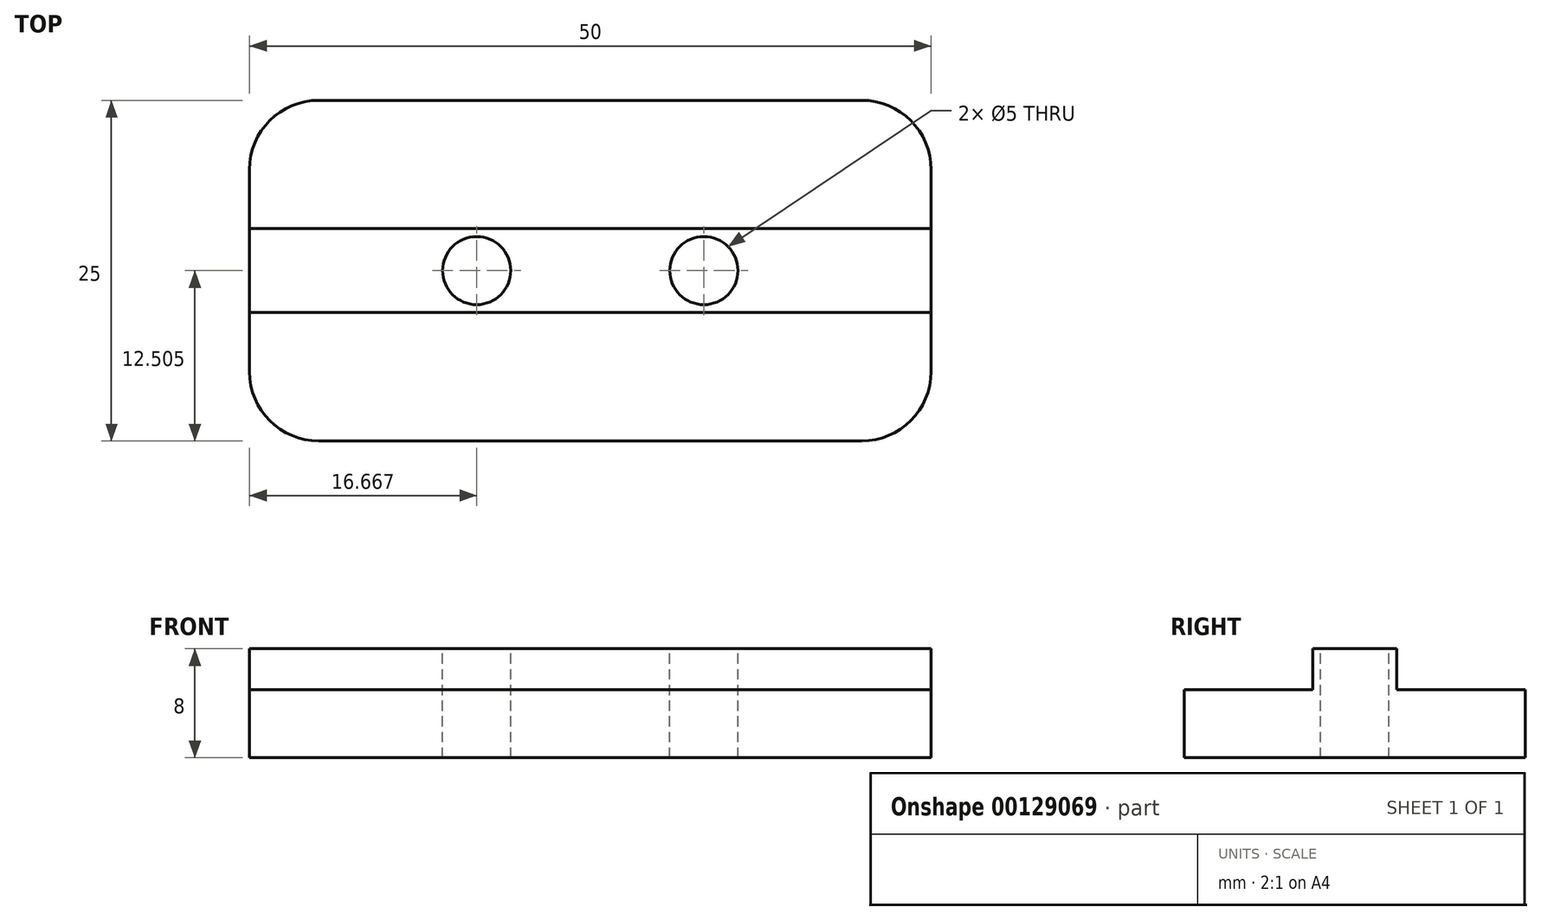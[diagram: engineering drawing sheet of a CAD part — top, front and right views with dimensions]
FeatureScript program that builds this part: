
annotation { "Feature Type Name" : "Feature", "Feature Type Description" : "" }
export const myFeature = defineFeature(function(context is Context, id is Id, definition is map)
    precondition{}
    {
        {
            var Q0;
            Q0=qCreatedBy(makeId("Right.planeOp"),FACE);
            var sketch = newSketch(context, id + "F0", { "sketchPlane" : qUnion([Q0])});
            skLineSegment(sketch, "E0", {"start": v(1.44, 11.02) * mm, "end": v(1.44, 14.02) * mm});
            skLineSegment(sketch, "E1", {"start": v(1.44, 14.02) * mm, "end": v(7.59, 14.02) * mm});
            skLineSegment(sketch, "E2", {"start": v(7.59, 14.02) * mm, "end": v(7.59, 11.02) * mm});
            skLineSegment(sketch, "E3", {"start": v(7.59, 11.02) * mm, "end": v(17.01, 11.02) * mm});
            skLineSegment(sketch, "E4", {"start": v(17.01, 11.02) * mm, "end": v(17.01, 6.02) * mm});
            skLineSegment(sketch, "E5", {"start": v(17.01, 6.02) * mm, "end": v(-7.99, 6.02) * mm});
            skLineSegment(sketch, "E6", {"start": v(-7.99, 6.02) * mm, "end": v(-7.99, 11.02) * mm});
            skLineSegment(sketch, "E7", {"start": v(-7.99, 11.02) * mm, "end": v(1.44, 11.02) * mm});
            skSolve(sketch);
        }
        {
            var Q0;
            Q0 = qSketchRegion(id + "F0", true);
            extrude(context, id + "F1", {"entities" : qUnion([Q0]), "depth" : 50 * mm});
        }
        {
            var Q0;
            Q0=makeQuery(id+"F1.opExtrude","CAP_EDGE",EDGE,{"disambiguationData":[OSD([sQuery(id+"F0.wireOp",EDGE,"E4")])],"isStart":false});
            var Q1;
            Q1=makeQuery(id+"F1.opExtrude","CAP_EDGE",EDGE,{"disambiguationData":[OSD([sQuery(id+"F0.wireOp",EDGE,"E6")])],"isStart":false});
            var Q2;
            Q2=makeQuery(id+"F1.opExtrude","CAP_EDGE",EDGE,{"disambiguationData":[OSD([sQuery(id+"F0.wireOp",EDGE,"E4")])],"isStart":true});
            var Q3;
            Q3=makeQuery(id+"F1.opExtrude","CAP_EDGE",EDGE,{"disambiguationData":[OSD([sQuery(id+"F0.wireOp",EDGE,"E6")])],"isStart":true});
            fillet(context, id + "F2", {"entities" : qUnion([Q0, Q1, Q2, Q3]), "radius" : 5.08 * mm, "tangentPropagation" : true, "allowEdgeOverflow" : false});
        }
        {
            var Q0;
            Q0=makeQuery(id+"F1.opExtrude","SWEPT_FACE",FACE,{"disambiguationData":[OSD([sQuery(id+"F0.wireOp",EDGE,"E1")])]});
            var sketch = newSketch(context, id + "F3", { "sketchPlane" : qUnion([Q0])});
            skPoint(sketch, "E8", {"position": v(16.67, 4.51) * mm});
            skPoint(sketch, "E9", {"position": v(33.33, 4.51) * mm});
            skSolve(sketch);
        }
        {
            var Q0;
            Q0=sQuery(id+"F3.wireOp",VERTEX,"E8");
            var Q1;
            Q1=sQuery(id+"F3.wireOp",VERTEX,"E9");
            var Q2;
            Q2=makeQuery(id+"F1.opExtrude","SWEPT_BODY",BODY,{"disambiguationData":[OSD([sQuery(id+"F0.wireOp",EDGE,"E0"),sQuery(id+"F0.wireOp",EDGE,"E1"),sQuery(id+"F0.wireOp",EDGE,"E2"),sQuery(id+"F0.wireOp",EDGE,"E3"),sQuery(id+"F0.wireOp",EDGE,"E4"),sQuery(id+"F0.wireOp",EDGE,"E5"),sQuery(id+"F0.wireOp",EDGE,"E6"),sQuery(id+"F0.wireOp",EDGE,"E7")])]});
            hole(context, id + "F4", {"style" : HoleStyle.SIMPLE, "endStyle" : HoleEndStyle.THROUGH, "holeDiameter" : 5 * mm, "locations" : qUnion([Q0, Q1]), "scope" : qUnion([Q2]), "isTappedThrough" : true});
        }
    });
